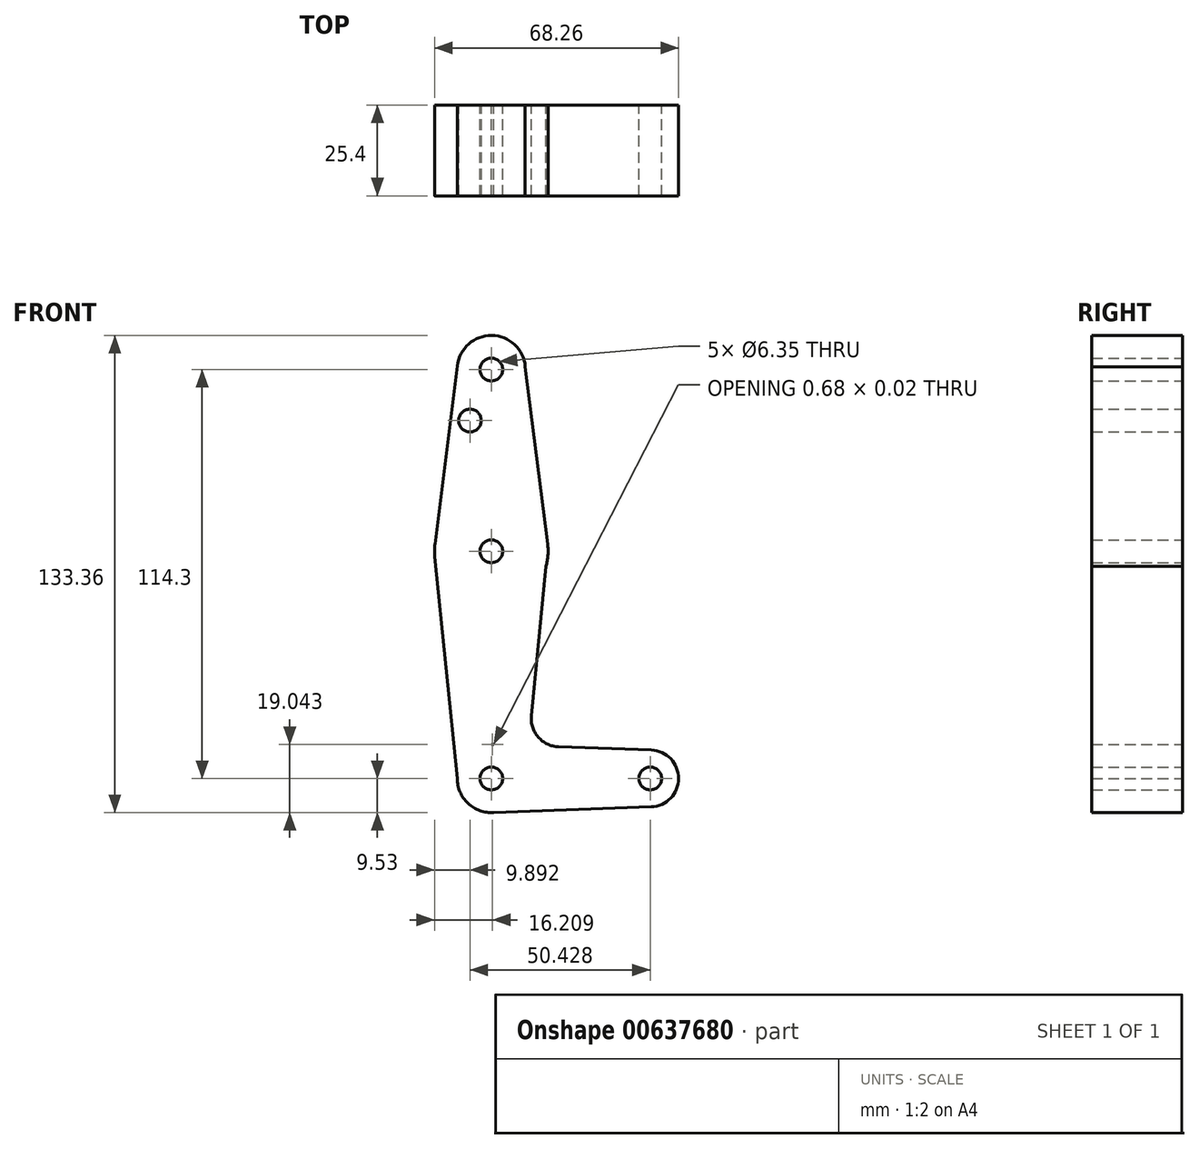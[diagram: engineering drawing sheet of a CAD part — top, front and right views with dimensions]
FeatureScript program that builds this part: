
annotation { "Feature Type Name" : "Feature", "Feature Type Description" : "" }
export const myFeature = defineFeature(function(context is Context, id is Id, definition is map)
    precondition{}
    {
        {
            var Q0;
            Q0=qCreatedBy(makeId("Front.planeOp"),FACE);
            var sketch = newSketch(context, id + "F0", { "sketchPlane" : qUnion([Q0])});
            skLineSegment(sketch, "E0", {"start": v(0, 0) * mm, "end": v(0, 114.3) * mm, "construction": true});
            skLineSegment(sketch, "E1", {"start": v(0, 0) * mm, "end": v(44.45, 0) * mm, "construction": true});
            skCircle(sketch, "E2", {"center": v(0, 114.3) * mm, "radius": 9.53 * mm});
            skCircle(sketch, "E3", {"center": v(0, 63.5) * mm, "radius": 15.88 * mm});
            skCircle(sketch, "E4", {"center": v(0, 0) * mm, "radius": 9.52 * mm});
            skCircle(sketch, "E5", {"center": v(44.45, 0) * mm, "radius": 7.94 * mm});
            skLineSegment(sketch, "E6", {"start": v(-9.47, 115.32) * mm, "end": v(-15.75, 65.48) * mm});
            skLineSegment(sketch, "E7", {"start": v(9.5, 115.1) * mm, "end": v(15.75, 65.48) * mm});
            skLineSegment(sketch, "E8", {"start": v(-9.52, 0) * mm, "end": v(-15.8, 61.9) * mm});
            skLineSegment(sketch, "E9", {"start": v(0, 9.52) * mm, "end": v(0.68, 9.5) * mm});
            skLineSegment(sketch, "E10", {"start": v(0, -9.52) * mm, "end": v(44.73, -7.93) * mm});
            skLineSegment(sketch, "E11.trimOffspring", {"start": v(18.83, 8.85) * mm, "end": v(44.73, 7.93) * mm});
            skCircle(sketch, "E12", {"center": v(0, 114.3) * mm, "radius": 3.18 * mm});
            skCircle(sketch, "E13", {"center": v(0, 63.5) * mm, "radius": 3.18 * mm});
            skCircle(sketch, "E14", {"center": v(44.45, 0) * mm, "radius": 3.18 * mm});
            skPoint(sketch, "E15.visualSharp", {"position": v(10.4, 9.15) * mm});
            skArc(sketch, "E15.filletArc", {"start": v(11.2, 17.55) * mm, "mid": v(13.13, 11.56) * mm, "end": v(18.83, 8.85) * mm});
            skCircle(sketch, "E16", {"center": v(-5.98, 100.03) * mm, "radius": 3.18 * mm});
            skLineSegment(sketch, "E17", {"start": v(15.3, 59.27) * mm, "end": v(11.2, 17.55) * mm});
            skCircle(sketch, "E18", {"center": v(0, 0) * mm, "radius": 3.18 * mm});
            skSolve(sketch);
        }
        {
            var Q0;
            Q0 = qSketchRegion(id + "F0", true);
            extrude(context, id + "F1", {"entities" : qUnion([Q0]), "depth" : 25.4 * mm, "offsetDistance" : 25.4 * mm});
        }
    });
